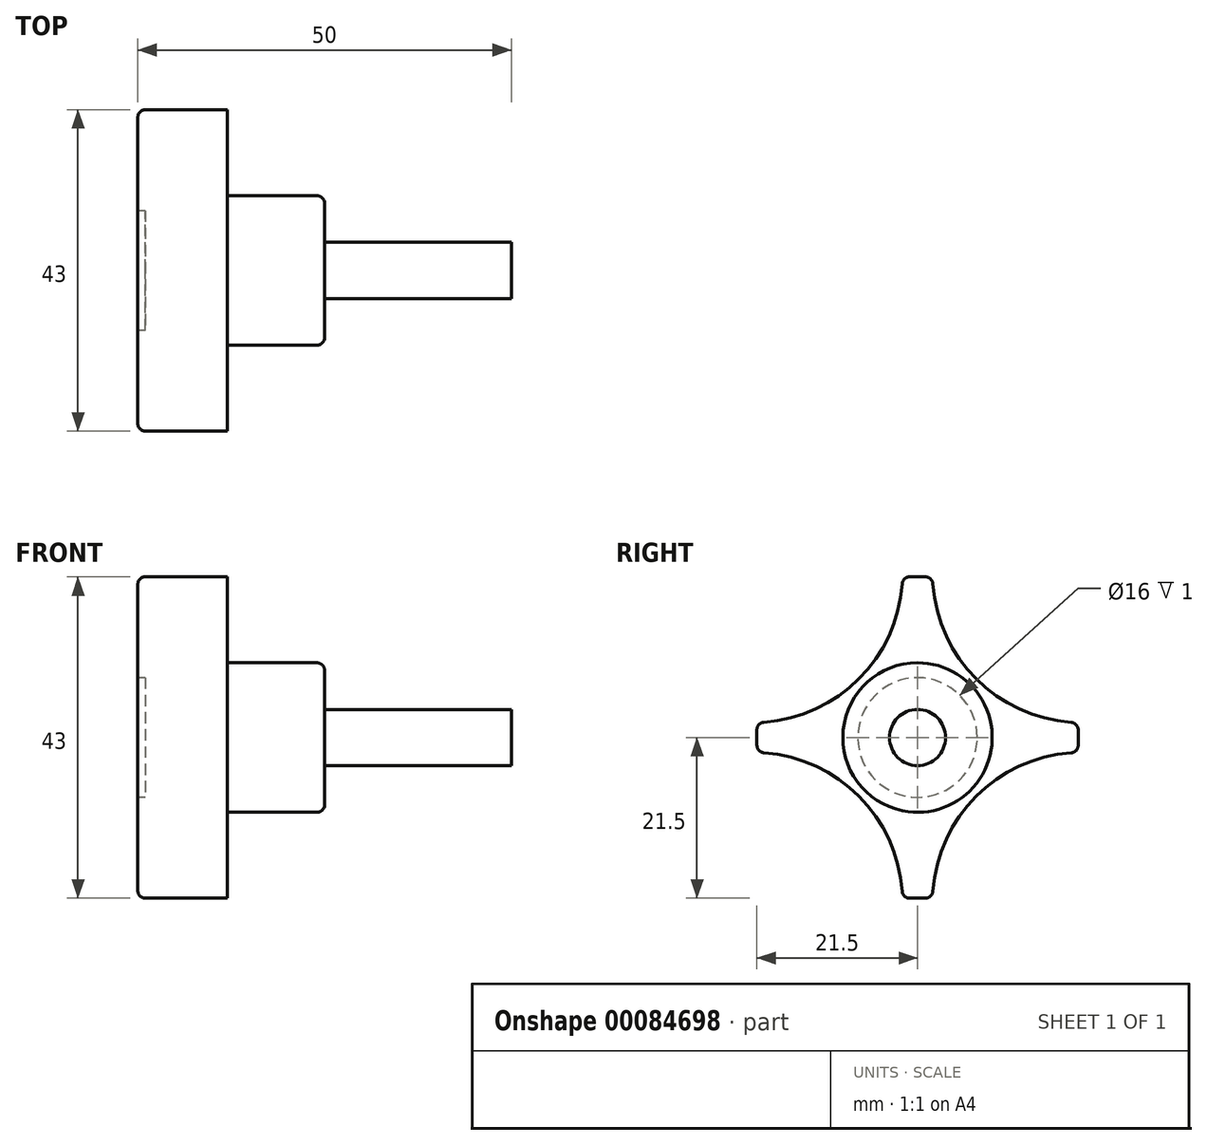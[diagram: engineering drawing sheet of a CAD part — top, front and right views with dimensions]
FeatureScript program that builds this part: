
annotation { "Feature Type Name" : "Feature", "Feature Type Description" : "" }
export const myFeature = defineFeature(function(context is Context, id is Id, definition is map)
    precondition{}
    {
        {
            var Q0;
            Q0=qCreatedBy(makeId("Right.planeOp"),FACE);
            var sketch = newSketch(context, id + "F0", { "sketchPlane" : qUnion([Q0])});
            skCircle(sketch, "E0", {"center": v(0, 0) * mm, "radius": 3.75 * mm});
            skSolve(sketch);
        }
        {
            var Q0;
            Q0 = qSketchRegion(id + "F0", true);
            extrude(context, id + "F1", {"entities" : qUnion([Q0]), "oppositeDirection" : true, "depth" : 25 * mm});
        }
        {
            var Q0;
            Q0=makeQuery(id+"F1.opExtrude","CAP_FACE",FACE,{"disambiguationData":[OSD([sQuery(id+"F0.wireOp",EDGE,"E0")])],"isStart":false});
            var sketch = newSketch(context, id + "F2", { "sketchPlane" : qUnion([Q0])});
            skCircle(sketch, "E1", {"center": v(0, 0) * mm, "radius": 10 * mm});
            skSolve(sketch);
        }
        {
            var Q0;
            Q0 = qSketchRegion(id + "F2", true);
            extrude(context, id + "F3", {"entities" : qUnion([Q0]), "operationType" : NewBodyOperationType.ADD, "depth" : 13 * mm});
        }
        {
            var Q0;
            Q0=makeQuery(id+"F3.opExtrude","CAP_FACE",FACE,{"disambiguationData":[OSD([sQuery(id+"F2.wireOp",EDGE,"E1")])],"isStart":false});
            var sketch = newSketch(context, id + "F4", { "sketchPlane" : qUnion([Q0])});
            skPoint(sketch, "E2", {"position": v(-2, 21.5) * mm});
            skLineSegment(sketch, "E3", {"start": v(-2, 21.5) * mm, "end": v(-2, 0) * mm});
            skLineSegment(sketch, "E4", {"start": v(-2, 21.5) * mm, "end": v(2, 21.5) * mm});
            skLineSegment(sketch, "E5", {"start": v(2, 21.5) * mm, "end": v(2, 0) * mm});
            skLineSegment(sketch, "E6.1.0", {"start": v(-21.5, -2) * mm, "end": v(0, -2) * mm});
            skLineSegment(sketch, "E6.1.1", {"start": v(-21.5, 2) * mm, "end": v(0, 2) * mm});
            skLineSegment(sketch, "E6.1.2", {"start": v(-21.5, -2) * mm, "end": v(-21.5, 2) * mm});
            skLineSegment(sketch, "E6.2.0", {"start": v(2, -21.5) * mm, "end": v(2, 0) * mm});
            skLineSegment(sketch, "E6.2.1", {"start": v(-2, -21.5) * mm, "end": v(-2, 0) * mm});
            skLineSegment(sketch, "E6.2.2", {"start": v(2, -21.5) * mm, "end": v(-2, -21.5) * mm});
            skLineSegment(sketch, "E6.3.0", {"start": v(21.5, 2) * mm, "end": v(0, 2) * mm});
            skLineSegment(sketch, "E6.3.1", {"start": v(21.5, -2) * mm, "end": v(0, -2) * mm});
            skLineSegment(sketch, "E6.3.2", {"start": v(21.5, 2) * mm, "end": v(21.5, -2) * mm});
            skPoint(sketch, "E6.center", {"position": v(0, 0) * mm});
            skSolve(sketch);
        }
        {
            var Q0;
            {var subQ0=sQuery(id+"F4.wireOp",EDGE,"E4");Q0=makeQuery(id+"F4.imprint","IMPRINT",FACE,{"disambiguationData":[TD([[makeQuery(id+"F4.imprint","IMPRINT",EDGE,{"derivedFrom":subQ0}),-1.0]])]});}
            var Q1;
            {var subQ1=sQuery(id+"F4.wireOp",EDGE,"E6.1.1");var subQ3=sQuery(id+"F4.wireOp",EDGE,"E3");var subQ4=makeQuery(id+"F4.imprint","INTERSECT",VERTEX,{"derivedFrom":[subQ3,subQ1]});Q1=makeQuery(id+"F4.imprint","IMPRINT",FACE,{"disambiguationData":[TD([[makeQuery(id+"F4.imprint","IMPRINT",EDGE,{"disambiguationData":[TD([[subQ4,1.0]])],"derivedFrom":subQ3}),1.0]])]});}
            var Q2;
            {var subQ1=sQuery(id+"F4.wireOp",EDGE,"E3");var subQ5=sQuery(id+"F4.wireOp",EDGE,"E6.2.1");var subQ6=makeQuery(id+"F4.imprint","INTERSECT",VERTEX,{"derivedFrom":[subQ1,subQ5]});Q2=makeQuery(id+"F4.imprint","IMPRINT",FACE,{"disambiguationData":[TD([[makeQuery(id+"F4.imprint","IMPRINT",EDGE,{"disambiguationData":[TD([[subQ6,1.0]])],"derivedFrom":subQ1}),-1.0]])]});}
            var Q3;
            {var subQ0=sQuery(id+"F4.wireOp",EDGE,"E6.1.2");Q3=makeQuery(id+"F4.imprint","IMPRINT",FACE,{"disambiguationData":[TD([[makeQuery(id+"F4.imprint","IMPRINT",EDGE,{"derivedFrom":subQ0}),-1.0]])]});}
            var Q4;
            {var subQ1=sQuery(id+"F4.wireOp",EDGE,"E6.1.0");var subQ7=sQuery(id+"F4.wireOp",EDGE,"E6.3.1");var subQ8=makeQuery(id+"F4.imprint","INTERSECT",VERTEX,{"derivedFrom":[subQ1,subQ7]});Q4=makeQuery(id+"F4.imprint","IMPRINT",FACE,{"disambiguationData":[TD([[makeQuery(id+"F4.imprint","IMPRINT",EDGE,{"disambiguationData":[TD([[subQ8,1.0]])],"derivedFrom":subQ1}),-1.0]])]});}
            var Q5;
            {var subQ3=sQuery(id+"F4.wireOp",EDGE,"E3");var subQ8=sQuery(id+"F4.wireOp",EDGE,"E6.2.1");var subQ14=makeQuery(id+"F4.imprint","INTERSECT",VERTEX,{"derivedFrom":[subQ3,subQ8]});Q5=makeQuery(id+"F4.imprint","IMPRINT",FACE,{"disambiguationData":[TD([[makeQuery(id+"F4.imprint","IMPRINT",EDGE,{"disambiguationData":[TD([[subQ14,1.0]])],"derivedFrom":subQ3}),1.0]])]});}
            var Q6;
            {var subQ1=sQuery(id+"F4.wireOp",EDGE,"E5");var subQ7=sQuery(id+"F4.wireOp",EDGE,"E6.2.0");var subQ8=makeQuery(id+"F4.imprint","INTERSECT",VERTEX,{"derivedFrom":[subQ1,subQ7]});Q6=makeQuery(id+"F4.imprint","IMPRINT",FACE,{"disambiguationData":[TD([[makeQuery(id+"F4.imprint","IMPRINT",EDGE,{"disambiguationData":[TD([[subQ8,1.0]])],"derivedFrom":subQ1}),1.0]])]});}
            var Q7;
            {var subQ0=sQuery(id+"F4.wireOp",EDGE,"E6.3.2");Q7=makeQuery(id+"F4.imprint","IMPRINT",FACE,{"disambiguationData":[TD([[makeQuery(id+"F4.imprint","IMPRINT",EDGE,{"derivedFrom":subQ0}),-1.0]])]});}
            var Q8;
            {var subQ0=sQuery(id+"F4.wireOp",EDGE,"E6.2.2");Q8=makeQuery(id+"F4.imprint","IMPRINT",FACE,{"disambiguationData":[TD([[makeQuery(id+"F4.imprint","IMPRINT",EDGE,{"derivedFrom":subQ0}),-1.0]])]});}
            extrude(context, id + "F5", {"entities" : qUnion([Q0, Q1, Q2, Q3, Q4, Q5, Q6, Q7, Q8]), "operationType" : NewBodyOperationType.ADD, "depth" : 12 * mm});
        }
        {
            var Q0;
            Q0=makeQuery(id+"F5.opExtrude","SWEPT_EDGE",EDGE,{"disambiguationData":[OSD([sQuery(id+"F4.wireOp",EDGE,"E6.1.0"),sQuery(id+"F4.wireOp",EDGE,"E6.2.1")])]});
            var Q1;
            Q1=makeQuery(id+"F5.opExtrude","SWEPT_EDGE",EDGE,{"disambiguationData":[OSD([sQuery(id+"F4.wireOp",EDGE,"E6.2.0"),sQuery(id+"F4.wireOp",EDGE,"E6.3.1")])]});
            var Q2;
            Q2=makeQuery(id+"F5.opExtrude","SWEPT_EDGE",EDGE,{"disambiguationData":[OSD([sQuery(id+"F4.wireOp",EDGE,"E5"),sQuery(id+"F4.wireOp",EDGE,"E6.3.0")])]});
            var Q3;
            Q3=makeQuery(id+"F5.opExtrude","SWEPT_EDGE",EDGE,{"disambiguationData":[OSD([sQuery(id+"F4.wireOp",EDGE,"E3"),sQuery(id+"F4.wireOp",EDGE,"E6.1.1")])]});
            fillet(context, id + "F6", {"entities" : qUnion([Q0, Q1, Q2, Q3]), "radius" : 20 * mm, "tangentPropagation" : true, "allowEdgeOverflow" : false});
        }
        {
            var Q0;
            Q0=makeQuery(id+"F6.opFillet","BLEND_EDGE",EDGE,{"blendedFrom":[makeQuery(id+"F5.opExtrude","SWEPT_EDGE",EDGE,{"disambiguationData":[OSD([sQuery(id+"F4.wireOp",EDGE,"E3"),sQuery(id+"F4.wireOp",EDGE,"E6.1.1")])]}),makeQuery(id+"F5.opExtrude","SWEPT_FACE",FACE,{"disambiguationData":[OSD([sQuery(id+"F4.wireOp",EDGE,"E4")])]})],"blendedInto":[makeQuery(id+"F5.opExtrude","SWEPT_FACE",FACE,{"disambiguationData":[OSD([sQuery(id+"F4.wireOp",EDGE,"E4")])]})]});
            var Q1;
            Q1=makeQuery(id+"F6.opFillet","BLEND_EDGE",EDGE,{"blendedFrom":[makeQuery(id+"F5.opExtrude","SWEPT_EDGE",EDGE,{"disambiguationData":[OSD([sQuery(id+"F4.wireOp",EDGE,"E5"),sQuery(id+"F4.wireOp",EDGE,"E6.3.0")])]}),makeQuery(id+"F5.opExtrude","SWEPT_FACE",FACE,{"disambiguationData":[OSD([sQuery(id+"F4.wireOp",EDGE,"E4")])]})],"blendedInto":[makeQuery(id+"F5.opExtrude","SWEPT_FACE",FACE,{"disambiguationData":[OSD([sQuery(id+"F4.wireOp",EDGE,"E4")])]})]});
            var Q2;
            Q2=makeQuery(id+"F6.opFillet","BLEND_EDGE",EDGE,{"blendedFrom":[makeQuery(id+"F5.opExtrude","SWEPT_EDGE",EDGE,{"disambiguationData":[OSD([sQuery(id+"F4.wireOp",EDGE,"E5"),sQuery(id+"F4.wireOp",EDGE,"E6.3.0")])]}),makeQuery(id+"F5.opExtrude","SWEPT_FACE",FACE,{"disambiguationData":[OSD([sQuery(id+"F4.wireOp",EDGE,"E6.3.2")])]})],"blendedInto":[makeQuery(id+"F5.opExtrude","SWEPT_FACE",FACE,{"disambiguationData":[OSD([sQuery(id+"F4.wireOp",EDGE,"E6.3.2")])]})]});
            var Q3;
            Q3=makeQuery(id+"F6.opFillet","BLEND_EDGE",EDGE,{"blendedFrom":[makeQuery(id+"F5.opExtrude","SWEPT_EDGE",EDGE,{"disambiguationData":[OSD([sQuery(id+"F4.wireOp",EDGE,"E3"),sQuery(id+"F4.wireOp",EDGE,"E6.1.1")])]}),makeQuery(id+"F5.opExtrude","SWEPT_FACE",FACE,{"disambiguationData":[OSD([sQuery(id+"F4.wireOp",EDGE,"E6.1.2")])]})],"blendedInto":[makeQuery(id+"F5.opExtrude","SWEPT_FACE",FACE,{"disambiguationData":[OSD([sQuery(id+"F4.wireOp",EDGE,"E6.1.2")])]})]});
            var Q4;
            Q4=makeQuery(id+"F6.opFillet","BLEND_EDGE",EDGE,{"blendedFrom":[makeQuery(id+"F5.opExtrude","SWEPT_EDGE",EDGE,{"disambiguationData":[OSD([sQuery(id+"F4.wireOp",EDGE,"E6.1.0"),sQuery(id+"F4.wireOp",EDGE,"E6.2.1")])]}),makeQuery(id+"F5.opExtrude","SWEPT_FACE",FACE,{"disambiguationData":[OSD([sQuery(id+"F4.wireOp",EDGE,"E6.1.2")])]})],"blendedInto":[makeQuery(id+"F5.opExtrude","SWEPT_FACE",FACE,{"disambiguationData":[OSD([sQuery(id+"F4.wireOp",EDGE,"E6.1.2")])]})]});
            var Q5;
            Q5=makeQuery(id+"F6.opFillet","BLEND_EDGE",EDGE,{"blendedFrom":[makeQuery(id+"F5.opExtrude","SWEPT_EDGE",EDGE,{"disambiguationData":[OSD([sQuery(id+"F4.wireOp",EDGE,"E6.1.0"),sQuery(id+"F4.wireOp",EDGE,"E6.2.1")])]}),makeQuery(id+"F5.opExtrude","SWEPT_FACE",FACE,{"disambiguationData":[OSD([sQuery(id+"F4.wireOp",EDGE,"E6.2.2")])]})],"blendedInto":[makeQuery(id+"F5.opExtrude","SWEPT_FACE",FACE,{"disambiguationData":[OSD([sQuery(id+"F4.wireOp",EDGE,"E6.2.2")])]})]});
            var Q6;
            Q6=makeQuery(id+"F6.opFillet","BLEND_EDGE",EDGE,{"blendedFrom":[makeQuery(id+"F5.opExtrude","SWEPT_EDGE",EDGE,{"disambiguationData":[OSD([sQuery(id+"F4.wireOp",EDGE,"E6.2.0"),sQuery(id+"F4.wireOp",EDGE,"E6.3.1")])]}),makeQuery(id+"F5.opExtrude","SWEPT_FACE",FACE,{"disambiguationData":[OSD([sQuery(id+"F4.wireOp",EDGE,"E6.3.2")])]})],"blendedInto":[makeQuery(id+"F5.opExtrude","SWEPT_FACE",FACE,{"disambiguationData":[OSD([sQuery(id+"F4.wireOp",EDGE,"E6.3.2")])]})]});
            var Q7;
            Q7=makeQuery(id+"F6.opFillet","BLEND_EDGE",EDGE,{"blendedFrom":[makeQuery(id+"F5.opExtrude","SWEPT_EDGE",EDGE,{"disambiguationData":[OSD([sQuery(id+"F4.wireOp",EDGE,"E6.2.0"),sQuery(id+"F4.wireOp",EDGE,"E6.3.1")])]}),makeQuery(id+"F5.opExtrude","SWEPT_FACE",FACE,{"disambiguationData":[OSD([sQuery(id+"F4.wireOp",EDGE,"E6.2.2")])]})],"blendedInto":[makeQuery(id+"F5.opExtrude","SWEPT_FACE",FACE,{"disambiguationData":[OSD([sQuery(id+"F4.wireOp",EDGE,"E6.2.2")])]})]});
            fillet(context, id + "F7", {"entities" : qUnion([Q0, Q1, Q2, Q3, Q4, Q5, Q6, Q7]), "radius" : 1 * mm, "tangentPropagation" : true, "allowEdgeOverflow" : false});
        }
        {
            var Q0;
            Q0=makeQuery(id+"F3.opExtrude","CAP_EDGE",EDGE,{"disambiguationData":[OSD([sQuery(id+"F2.wireOp",EDGE,"E1")])],"isStart":true});
            fillet(context, id + "F8", {"entities" : qUnion([Q0]), "radius" : 1 * mm, "tangentPropagation" : true, "allowEdgeOverflow" : false});
        }
        {
            var Q0;
            Q0=makeQuery(id+"F5.opExtrude","CAP_FACE",FACE,{"disambiguationData":[OSD([sQuery(id+"F4.wireOp",EDGE,"E3"),sQuery(id+"F4.wireOp",EDGE,"E4"),sQuery(id+"F4.wireOp",EDGE,"E5"),sQuery(id+"F4.wireOp",EDGE,"E6.1.0"),sQuery(id+"F4.wireOp",EDGE,"E6.1.1"),sQuery(id+"F4.wireOp",EDGE,"E6.1.2"),sQuery(id+"F4.wireOp",EDGE,"E6.2.0"),sQuery(id+"F4.wireOp",EDGE,"E6.2.1"),sQuery(id+"F4.wireOp",EDGE,"E6.2.2"),sQuery(id+"F4.wireOp",EDGE,"E6.3.0"),sQuery(id+"F4.wireOp",EDGE,"E6.3.1"),sQuery(id+"F4.wireOp",EDGE,"E6.3.2")])],"isStart":false});
            var sketch = newSketch(context, id + "F9", { "sketchPlane" : qUnion([Q0])});
            skCircle(sketch, "E7", {"center": v(0, 0) * mm, "radius": 8 * mm});
            skSolve(sketch);
        }
        {
            var Q0;
            Q0=makeQuery(id+"F9.imprint","IMPRINT",FACE,{"disambiguationData":[TD([[makeQuery(id+"F9.imprint","IMPRINT",EDGE,{"derivedFrom":sQuery(id+"F9.wireOp",EDGE,"E7")}),1.0]])]});
            extrude(context, id + "F10", {"entities" : qUnion([Q0]), "operationType" : NewBodyOperationType.REMOVE, "oppositeDirection" : true, "depth" : 1 * mm});
        }
        {
            var Q0;
            {var subQ0=sQuery(id+"F4.wireOp",EDGE,"E6.1.1");var subQ1=sQuery(id+"F4.wireOp",EDGE,"E3");Q0=makeQuery(id+"F6.opFillet","BLEND_EDGE",EDGE,{"blendedFrom":[makeQuery(id+"F5.opExtrude","SWEPT_EDGE",EDGE,{"disambiguationData":[OSD([subQ1,subQ0])]}),makeQuery(id+"F5.opExtrude","CAP_FACE",FACE,{"disambiguationData":[OSD([subQ1,sQuery(id+"F4.wireOp",EDGE,"E4"),sQuery(id+"F4.wireOp",EDGE,"E5"),sQuery(id+"F4.wireOp",EDGE,"E6.1.0"),subQ0,sQuery(id+"F4.wireOp",EDGE,"E6.1.2"),sQuery(id+"F4.wireOp",EDGE,"E6.2.0"),sQuery(id+"F4.wireOp",EDGE,"E6.2.1"),sQuery(id+"F4.wireOp",EDGE,"E6.2.2"),sQuery(id+"F4.wireOp",EDGE,"E6.3.0"),sQuery(id+"F4.wireOp",EDGE,"E6.3.1"),sQuery(id+"F4.wireOp",EDGE,"E6.3.2")])],"isStart":false})],"blendedInto":[makeQuery(id+"F5.opExtrude","CAP_FACE",FACE,{"disambiguationData":[OSD([subQ1,sQuery(id+"F4.wireOp",EDGE,"E4"),sQuery(id+"F4.wireOp",EDGE,"E5"),sQuery(id+"F4.wireOp",EDGE,"E6.1.0"),subQ0,sQuery(id+"F4.wireOp",EDGE,"E6.1.2"),sQuery(id+"F4.wireOp",EDGE,"E6.2.0"),sQuery(id+"F4.wireOp",EDGE,"E6.2.1"),sQuery(id+"F4.wireOp",EDGE,"E6.2.2"),sQuery(id+"F4.wireOp",EDGE,"E6.3.0"),sQuery(id+"F4.wireOp",EDGE,"E6.3.1"),sQuery(id+"F4.wireOp",EDGE,"E6.3.2")])],"isStart":false})]});}
            var Q1;
            {var subQ0=sQuery(id+"F4.wireOp",EDGE,"E6.3.0");var subQ1=sQuery(id+"F4.wireOp",EDGE,"E5");Q1=makeQuery(id+"F6.opFillet","BLEND_EDGE",EDGE,{"blendedFrom":[makeQuery(id+"F5.opExtrude","SWEPT_EDGE",EDGE,{"disambiguationData":[OSD([subQ1,subQ0])]}),makeQuery(id+"F5.opExtrude","CAP_FACE",FACE,{"disambiguationData":[OSD([sQuery(id+"F4.wireOp",EDGE,"E3"),sQuery(id+"F4.wireOp",EDGE,"E4"),subQ1,sQuery(id+"F4.wireOp",EDGE,"E6.1.0"),sQuery(id+"F4.wireOp",EDGE,"E6.1.1"),sQuery(id+"F4.wireOp",EDGE,"E6.1.2"),sQuery(id+"F4.wireOp",EDGE,"E6.2.0"),sQuery(id+"F4.wireOp",EDGE,"E6.2.1"),sQuery(id+"F4.wireOp",EDGE,"E6.2.2"),subQ0,sQuery(id+"F4.wireOp",EDGE,"E6.3.1"),sQuery(id+"F4.wireOp",EDGE,"E6.3.2")])],"isStart":false})],"blendedInto":[makeQuery(id+"F5.opExtrude","CAP_FACE",FACE,{"disambiguationData":[OSD([sQuery(id+"F4.wireOp",EDGE,"E3"),sQuery(id+"F4.wireOp",EDGE,"E4"),subQ1,sQuery(id+"F4.wireOp",EDGE,"E6.1.0"),sQuery(id+"F4.wireOp",EDGE,"E6.1.1"),sQuery(id+"F4.wireOp",EDGE,"E6.1.2"),sQuery(id+"F4.wireOp",EDGE,"E6.2.0"),sQuery(id+"F4.wireOp",EDGE,"E6.2.1"),sQuery(id+"F4.wireOp",EDGE,"E6.2.2"),subQ0,sQuery(id+"F4.wireOp",EDGE,"E6.3.1"),sQuery(id+"F4.wireOp",EDGE,"E6.3.2")])],"isStart":false})]});}
            var Q2;
            {var subQ0=sQuery(id+"F4.wireOp",EDGE,"E6.3.1");var subQ1=sQuery(id+"F4.wireOp",EDGE,"E6.2.0");Q2=makeQuery(id+"F6.opFillet","BLEND_EDGE",EDGE,{"blendedFrom":[makeQuery(id+"F5.opExtrude","SWEPT_EDGE",EDGE,{"disambiguationData":[OSD([subQ1,subQ0])]}),makeQuery(id+"F5.opExtrude","CAP_FACE",FACE,{"disambiguationData":[OSD([sQuery(id+"F4.wireOp",EDGE,"E3"),sQuery(id+"F4.wireOp",EDGE,"E4"),sQuery(id+"F4.wireOp",EDGE,"E5"),sQuery(id+"F4.wireOp",EDGE,"E6.1.0"),sQuery(id+"F4.wireOp",EDGE,"E6.1.1"),sQuery(id+"F4.wireOp",EDGE,"E6.1.2"),subQ1,sQuery(id+"F4.wireOp",EDGE,"E6.2.1"),sQuery(id+"F4.wireOp",EDGE,"E6.2.2"),sQuery(id+"F4.wireOp",EDGE,"E6.3.0"),subQ0,sQuery(id+"F4.wireOp",EDGE,"E6.3.2")])],"isStart":false})],"blendedInto":[makeQuery(id+"F5.opExtrude","CAP_FACE",FACE,{"disambiguationData":[OSD([sQuery(id+"F4.wireOp",EDGE,"E3"),sQuery(id+"F4.wireOp",EDGE,"E4"),sQuery(id+"F4.wireOp",EDGE,"E5"),sQuery(id+"F4.wireOp",EDGE,"E6.1.0"),sQuery(id+"F4.wireOp",EDGE,"E6.1.1"),sQuery(id+"F4.wireOp",EDGE,"E6.1.2"),subQ1,sQuery(id+"F4.wireOp",EDGE,"E6.2.1"),sQuery(id+"F4.wireOp",EDGE,"E6.2.2"),sQuery(id+"F4.wireOp",EDGE,"E6.3.0"),subQ0,sQuery(id+"F4.wireOp",EDGE,"E6.3.2")])],"isStart":false})]});}
            var Q3;
            {var subQ0=sQuery(id+"F4.wireOp",EDGE,"E6.2.1");var subQ1=sQuery(id+"F4.wireOp",EDGE,"E6.1.0");Q3=makeQuery(id+"F6.opFillet","BLEND_EDGE",EDGE,{"blendedFrom":[makeQuery(id+"F5.opExtrude","SWEPT_EDGE",EDGE,{"disambiguationData":[OSD([subQ1,subQ0])]}),makeQuery(id+"F5.opExtrude","CAP_FACE",FACE,{"disambiguationData":[OSD([sQuery(id+"F4.wireOp",EDGE,"E3"),sQuery(id+"F4.wireOp",EDGE,"E4"),sQuery(id+"F4.wireOp",EDGE,"E5"),subQ1,sQuery(id+"F4.wireOp",EDGE,"E6.1.1"),sQuery(id+"F4.wireOp",EDGE,"E6.1.2"),sQuery(id+"F4.wireOp",EDGE,"E6.2.0"),subQ0,sQuery(id+"F4.wireOp",EDGE,"E6.2.2"),sQuery(id+"F4.wireOp",EDGE,"E6.3.0"),sQuery(id+"F4.wireOp",EDGE,"E6.3.1"),sQuery(id+"F4.wireOp",EDGE,"E6.3.2")])],"isStart":false})],"blendedInto":[makeQuery(id+"F5.opExtrude","CAP_FACE",FACE,{"disambiguationData":[OSD([sQuery(id+"F4.wireOp",EDGE,"E3"),sQuery(id+"F4.wireOp",EDGE,"E4"),sQuery(id+"F4.wireOp",EDGE,"E5"),subQ1,sQuery(id+"F4.wireOp",EDGE,"E6.1.1"),sQuery(id+"F4.wireOp",EDGE,"E6.1.2"),sQuery(id+"F4.wireOp",EDGE,"E6.2.0"),subQ0,sQuery(id+"F4.wireOp",EDGE,"E6.2.2"),sQuery(id+"F4.wireOp",EDGE,"E6.3.0"),sQuery(id+"F4.wireOp",EDGE,"E6.3.1"),sQuery(id+"F4.wireOp",EDGE,"E6.3.2")])],"isStart":false})]});}
            var Q4;
            {var subQ0=sQuery(id+"F4.wireOp",EDGE,"E6.1.1");var subQ1=sQuery(id+"F4.wireOp",EDGE,"E4");var subQ2=sQuery(id+"F4.wireOp",EDGE,"E3");Q4=makeQuery(id+"F7.opFillet","BLEND_EDGE",EDGE,{"blendedFrom":[makeQuery(id+"F6.opFillet","BLEND_EDGE",EDGE,{"blendedFrom":[makeQuery(id+"F5.opExtrude","SWEPT_EDGE",EDGE,{"disambiguationData":[OSD([subQ2,subQ0])]}),makeQuery(id+"F5.opExtrude","SWEPT_FACE",FACE,{"disambiguationData":[OSD([subQ1])]})],"blendedInto":[makeQuery(id+"F5.opExtrude","SWEPT_FACE",FACE,{"disambiguationData":[OSD([subQ1])]})]}),makeQuery(id+"F5.opExtrude","CAP_FACE",FACE,{"disambiguationData":[OSD([subQ2,subQ1,sQuery(id+"F4.wireOp",EDGE,"E5"),sQuery(id+"F4.wireOp",EDGE,"E6.1.0"),subQ0,sQuery(id+"F4.wireOp",EDGE,"E6.1.2"),sQuery(id+"F4.wireOp",EDGE,"E6.2.0"),sQuery(id+"F4.wireOp",EDGE,"E6.2.1"),sQuery(id+"F4.wireOp",EDGE,"E6.2.2"),sQuery(id+"F4.wireOp",EDGE,"E6.3.0"),sQuery(id+"F4.wireOp",EDGE,"E6.3.1"),sQuery(id+"F4.wireOp",EDGE,"E6.3.2")])],"isStart":false})],"blendedInto":[makeQuery(id+"F5.opExtrude","CAP_FACE",FACE,{"disambiguationData":[OSD([subQ2,subQ1,sQuery(id+"F4.wireOp",EDGE,"E5"),sQuery(id+"F4.wireOp",EDGE,"E6.1.0"),subQ0,sQuery(id+"F4.wireOp",EDGE,"E6.1.2"),sQuery(id+"F4.wireOp",EDGE,"E6.2.0"),sQuery(id+"F4.wireOp",EDGE,"E6.2.1"),sQuery(id+"F4.wireOp",EDGE,"E6.2.2"),sQuery(id+"F4.wireOp",EDGE,"E6.3.0"),sQuery(id+"F4.wireOp",EDGE,"E6.3.1"),sQuery(id+"F4.wireOp",EDGE,"E6.3.2")])],"isStart":false})]});}
            var Q5;
            Q5=makeQuery(id+"F5.opExtrude","CAP_EDGE",EDGE,{"disambiguationData":[OSD([sQuery(id+"F4.wireOp",EDGE,"E6.3.2")])],"isStart":false});
            var Q6;
            {var subQ0=sQuery(id+"F4.wireOp",EDGE,"E6.3.0");var subQ1=sQuery(id+"F4.wireOp",EDGE,"E5");var subQ2=sQuery(id+"F4.wireOp",EDGE,"E4");Q6=makeQuery(id+"F7.opFillet","BLEND_EDGE",EDGE,{"blendedFrom":[makeQuery(id+"F6.opFillet","BLEND_EDGE",EDGE,{"blendedFrom":[makeQuery(id+"F5.opExtrude","SWEPT_EDGE",EDGE,{"disambiguationData":[OSD([subQ1,subQ0])]}),makeQuery(id+"F5.opExtrude","SWEPT_FACE",FACE,{"disambiguationData":[OSD([subQ2])]})],"blendedInto":[makeQuery(id+"F5.opExtrude","SWEPT_FACE",FACE,{"disambiguationData":[OSD([subQ2])]})]}),makeQuery(id+"F5.opExtrude","CAP_FACE",FACE,{"disambiguationData":[OSD([sQuery(id+"F4.wireOp",EDGE,"E3"),subQ2,subQ1,sQuery(id+"F4.wireOp",EDGE,"E6.1.0"),sQuery(id+"F4.wireOp",EDGE,"E6.1.1"),sQuery(id+"F4.wireOp",EDGE,"E6.1.2"),sQuery(id+"F4.wireOp",EDGE,"E6.2.0"),sQuery(id+"F4.wireOp",EDGE,"E6.2.1"),sQuery(id+"F4.wireOp",EDGE,"E6.2.2"),subQ0,sQuery(id+"F4.wireOp",EDGE,"E6.3.1"),sQuery(id+"F4.wireOp",EDGE,"E6.3.2")])],"isStart":false})],"blendedInto":[makeQuery(id+"F5.opExtrude","CAP_FACE",FACE,{"disambiguationData":[OSD([sQuery(id+"F4.wireOp",EDGE,"E3"),subQ2,subQ1,sQuery(id+"F4.wireOp",EDGE,"E6.1.0"),sQuery(id+"F4.wireOp",EDGE,"E6.1.1"),sQuery(id+"F4.wireOp",EDGE,"E6.1.2"),sQuery(id+"F4.wireOp",EDGE,"E6.2.0"),sQuery(id+"F4.wireOp",EDGE,"E6.2.1"),sQuery(id+"F4.wireOp",EDGE,"E6.2.2"),subQ0,sQuery(id+"F4.wireOp",EDGE,"E6.3.1"),sQuery(id+"F4.wireOp",EDGE,"E6.3.2")])],"isStart":false})]});}
            var Q7;
            Q7=makeQuery(id+"F5.opExtrude","CAP_EDGE",EDGE,{"disambiguationData":[OSD([sQuery(id+"F4.wireOp",EDGE,"E4")])],"isStart":false});
            var Q8;
            {var subQ0=sQuery(id+"F4.wireOp",EDGE,"E6.2.1");var subQ1=sQuery(id+"F4.wireOp",EDGE,"E6.1.2");var subQ2=sQuery(id+"F4.wireOp",EDGE,"E6.1.0");Q8=makeQuery(id+"F7.opFillet","BLEND_EDGE",EDGE,{"blendedFrom":[makeQuery(id+"F6.opFillet","BLEND_EDGE",EDGE,{"blendedFrom":[makeQuery(id+"F5.opExtrude","SWEPT_EDGE",EDGE,{"disambiguationData":[OSD([subQ2,subQ0])]}),makeQuery(id+"F5.opExtrude","SWEPT_FACE",FACE,{"disambiguationData":[OSD([subQ1])]})],"blendedInto":[makeQuery(id+"F5.opExtrude","SWEPT_FACE",FACE,{"disambiguationData":[OSD([subQ1])]})]}),makeQuery(id+"F5.opExtrude","CAP_FACE",FACE,{"disambiguationData":[OSD([sQuery(id+"F4.wireOp",EDGE,"E3"),sQuery(id+"F4.wireOp",EDGE,"E4"),sQuery(id+"F4.wireOp",EDGE,"E5"),subQ2,sQuery(id+"F4.wireOp",EDGE,"E6.1.1"),subQ1,sQuery(id+"F4.wireOp",EDGE,"E6.2.0"),subQ0,sQuery(id+"F4.wireOp",EDGE,"E6.2.2"),sQuery(id+"F4.wireOp",EDGE,"E6.3.0"),sQuery(id+"F4.wireOp",EDGE,"E6.3.1"),sQuery(id+"F4.wireOp",EDGE,"E6.3.2")])],"isStart":false})],"blendedInto":[makeQuery(id+"F5.opExtrude","CAP_FACE",FACE,{"disambiguationData":[OSD([sQuery(id+"F4.wireOp",EDGE,"E3"),sQuery(id+"F4.wireOp",EDGE,"E4"),sQuery(id+"F4.wireOp",EDGE,"E5"),subQ2,sQuery(id+"F4.wireOp",EDGE,"E6.1.1"),subQ1,sQuery(id+"F4.wireOp",EDGE,"E6.2.0"),subQ0,sQuery(id+"F4.wireOp",EDGE,"E6.2.2"),sQuery(id+"F4.wireOp",EDGE,"E6.3.0"),sQuery(id+"F4.wireOp",EDGE,"E6.3.1"),sQuery(id+"F4.wireOp",EDGE,"E6.3.2")])],"isStart":false})]});}
            var Q9;
            Q9=makeQuery(id+"F5.opExtrude","CAP_EDGE",EDGE,{"disambiguationData":[OSD([sQuery(id+"F4.wireOp",EDGE,"E6.1.2")])],"isStart":false});
            var Q10;
            {var subQ0=sQuery(id+"F4.wireOp",EDGE,"E6.1.2");var subQ1=sQuery(id+"F4.wireOp",EDGE,"E6.1.1");var subQ2=sQuery(id+"F4.wireOp",EDGE,"E3");Q10=makeQuery(id+"F7.opFillet","BLEND_EDGE",EDGE,{"blendedFrom":[makeQuery(id+"F6.opFillet","BLEND_EDGE",EDGE,{"blendedFrom":[makeQuery(id+"F5.opExtrude","SWEPT_EDGE",EDGE,{"disambiguationData":[OSD([subQ2,subQ1])]}),makeQuery(id+"F5.opExtrude","SWEPT_FACE",FACE,{"disambiguationData":[OSD([subQ0])]})],"blendedInto":[makeQuery(id+"F5.opExtrude","SWEPT_FACE",FACE,{"disambiguationData":[OSD([subQ0])]})]}),makeQuery(id+"F5.opExtrude","CAP_FACE",FACE,{"disambiguationData":[OSD([subQ2,sQuery(id+"F4.wireOp",EDGE,"E4"),sQuery(id+"F4.wireOp",EDGE,"E5"),sQuery(id+"F4.wireOp",EDGE,"E6.1.0"),subQ1,subQ0,sQuery(id+"F4.wireOp",EDGE,"E6.2.0"),sQuery(id+"F4.wireOp",EDGE,"E6.2.1"),sQuery(id+"F4.wireOp",EDGE,"E6.2.2"),sQuery(id+"F4.wireOp",EDGE,"E6.3.0"),sQuery(id+"F4.wireOp",EDGE,"E6.3.1"),sQuery(id+"F4.wireOp",EDGE,"E6.3.2")])],"isStart":false})],"blendedInto":[makeQuery(id+"F5.opExtrude","CAP_FACE",FACE,{"disambiguationData":[OSD([subQ2,sQuery(id+"F4.wireOp",EDGE,"E4"),sQuery(id+"F4.wireOp",EDGE,"E5"),sQuery(id+"F4.wireOp",EDGE,"E6.1.0"),subQ1,subQ0,sQuery(id+"F4.wireOp",EDGE,"E6.2.0"),sQuery(id+"F4.wireOp",EDGE,"E6.2.1"),sQuery(id+"F4.wireOp",EDGE,"E6.2.2"),sQuery(id+"F4.wireOp",EDGE,"E6.3.0"),sQuery(id+"F4.wireOp",EDGE,"E6.3.1"),sQuery(id+"F4.wireOp",EDGE,"E6.3.2")])],"isStart":false})]});}
            var Q11;
            {var subQ0=sQuery(id+"F4.wireOp",EDGE,"E6.2.2");var subQ1=sQuery(id+"F4.wireOp",EDGE,"E6.2.1");var subQ2=sQuery(id+"F4.wireOp",EDGE,"E6.1.0");Q11=makeQuery(id+"F7.opFillet","BLEND_EDGE",EDGE,{"blendedFrom":[makeQuery(id+"F6.opFillet","BLEND_EDGE",EDGE,{"blendedFrom":[makeQuery(id+"F5.opExtrude","SWEPT_EDGE",EDGE,{"disambiguationData":[OSD([subQ2,subQ1])]}),makeQuery(id+"F5.opExtrude","SWEPT_FACE",FACE,{"disambiguationData":[OSD([subQ0])]})],"blendedInto":[makeQuery(id+"F5.opExtrude","SWEPT_FACE",FACE,{"disambiguationData":[OSD([subQ0])]})]}),makeQuery(id+"F5.opExtrude","CAP_FACE",FACE,{"disambiguationData":[OSD([sQuery(id+"F4.wireOp",EDGE,"E3"),sQuery(id+"F4.wireOp",EDGE,"E4"),sQuery(id+"F4.wireOp",EDGE,"E5"),subQ2,sQuery(id+"F4.wireOp",EDGE,"E6.1.1"),sQuery(id+"F4.wireOp",EDGE,"E6.1.2"),sQuery(id+"F4.wireOp",EDGE,"E6.2.0"),subQ1,subQ0,sQuery(id+"F4.wireOp",EDGE,"E6.3.0"),sQuery(id+"F4.wireOp",EDGE,"E6.3.1"),sQuery(id+"F4.wireOp",EDGE,"E6.3.2")])],"isStart":false})],"blendedInto":[makeQuery(id+"F5.opExtrude","CAP_FACE",FACE,{"disambiguationData":[OSD([sQuery(id+"F4.wireOp",EDGE,"E3"),sQuery(id+"F4.wireOp",EDGE,"E4"),sQuery(id+"F4.wireOp",EDGE,"E5"),subQ2,sQuery(id+"F4.wireOp",EDGE,"E6.1.1"),sQuery(id+"F4.wireOp",EDGE,"E6.1.2"),sQuery(id+"F4.wireOp",EDGE,"E6.2.0"),subQ1,subQ0,sQuery(id+"F4.wireOp",EDGE,"E6.3.0"),sQuery(id+"F4.wireOp",EDGE,"E6.3.1"),sQuery(id+"F4.wireOp",EDGE,"E6.3.2")])],"isStart":false})]});}
            var Q12;
            Q12=makeQuery(id+"F5.opExtrude","CAP_EDGE",EDGE,{"disambiguationData":[OSD([sQuery(id+"F4.wireOp",EDGE,"E6.2.2")])],"isStart":false});
            var Q13;
            {var subQ0=sQuery(id+"F4.wireOp",EDGE,"E6.3.1");var subQ1=sQuery(id+"F4.wireOp",EDGE,"E6.2.2");var subQ2=sQuery(id+"F4.wireOp",EDGE,"E6.2.0");Q13=makeQuery(id+"F7.opFillet","BLEND_EDGE",EDGE,{"blendedFrom":[makeQuery(id+"F6.opFillet","BLEND_EDGE",EDGE,{"blendedFrom":[makeQuery(id+"F5.opExtrude","SWEPT_EDGE",EDGE,{"disambiguationData":[OSD([subQ2,subQ0])]}),makeQuery(id+"F5.opExtrude","SWEPT_FACE",FACE,{"disambiguationData":[OSD([subQ1])]})],"blendedInto":[makeQuery(id+"F5.opExtrude","SWEPT_FACE",FACE,{"disambiguationData":[OSD([subQ1])]})]}),makeQuery(id+"F5.opExtrude","CAP_FACE",FACE,{"disambiguationData":[OSD([sQuery(id+"F4.wireOp",EDGE,"E3"),sQuery(id+"F4.wireOp",EDGE,"E4"),sQuery(id+"F4.wireOp",EDGE,"E5"),sQuery(id+"F4.wireOp",EDGE,"E6.1.0"),sQuery(id+"F4.wireOp",EDGE,"E6.1.1"),sQuery(id+"F4.wireOp",EDGE,"E6.1.2"),subQ2,sQuery(id+"F4.wireOp",EDGE,"E6.2.1"),subQ1,sQuery(id+"F4.wireOp",EDGE,"E6.3.0"),subQ0,sQuery(id+"F4.wireOp",EDGE,"E6.3.2")])],"isStart":false})],"blendedInto":[makeQuery(id+"F5.opExtrude","CAP_FACE",FACE,{"disambiguationData":[OSD([sQuery(id+"F4.wireOp",EDGE,"E3"),sQuery(id+"F4.wireOp",EDGE,"E4"),sQuery(id+"F4.wireOp",EDGE,"E5"),sQuery(id+"F4.wireOp",EDGE,"E6.1.0"),sQuery(id+"F4.wireOp",EDGE,"E6.1.1"),sQuery(id+"F4.wireOp",EDGE,"E6.1.2"),subQ2,sQuery(id+"F4.wireOp",EDGE,"E6.2.1"),subQ1,sQuery(id+"F4.wireOp",EDGE,"E6.3.0"),subQ0,sQuery(id+"F4.wireOp",EDGE,"E6.3.2")])],"isStart":false})]});}
            var Q14;
            {var subQ0=sQuery(id+"F4.wireOp",EDGE,"E6.3.2");var subQ1=sQuery(id+"F4.wireOp",EDGE,"E6.3.1");var subQ2=sQuery(id+"F4.wireOp",EDGE,"E6.2.0");Q14=makeQuery(id+"F7.opFillet","BLEND_EDGE",EDGE,{"blendedFrom":[makeQuery(id+"F6.opFillet","BLEND_EDGE",EDGE,{"blendedFrom":[makeQuery(id+"F5.opExtrude","SWEPT_EDGE",EDGE,{"disambiguationData":[OSD([subQ2,subQ1])]}),makeQuery(id+"F5.opExtrude","SWEPT_FACE",FACE,{"disambiguationData":[OSD([subQ0])]})],"blendedInto":[makeQuery(id+"F5.opExtrude","SWEPT_FACE",FACE,{"disambiguationData":[OSD([subQ0])]})]}),makeQuery(id+"F5.opExtrude","CAP_FACE",FACE,{"disambiguationData":[OSD([sQuery(id+"F4.wireOp",EDGE,"E3"),sQuery(id+"F4.wireOp",EDGE,"E4"),sQuery(id+"F4.wireOp",EDGE,"E5"),sQuery(id+"F4.wireOp",EDGE,"E6.1.0"),sQuery(id+"F4.wireOp",EDGE,"E6.1.1"),sQuery(id+"F4.wireOp",EDGE,"E6.1.2"),subQ2,sQuery(id+"F4.wireOp",EDGE,"E6.2.1"),sQuery(id+"F4.wireOp",EDGE,"E6.2.2"),sQuery(id+"F4.wireOp",EDGE,"E6.3.0"),subQ1,subQ0])],"isStart":false})],"blendedInto":[makeQuery(id+"F5.opExtrude","CAP_FACE",FACE,{"disambiguationData":[OSD([sQuery(id+"F4.wireOp",EDGE,"E3"),sQuery(id+"F4.wireOp",EDGE,"E4"),sQuery(id+"F4.wireOp",EDGE,"E5"),sQuery(id+"F4.wireOp",EDGE,"E6.1.0"),sQuery(id+"F4.wireOp",EDGE,"E6.1.1"),sQuery(id+"F4.wireOp",EDGE,"E6.1.2"),subQ2,sQuery(id+"F4.wireOp",EDGE,"E6.2.1"),sQuery(id+"F4.wireOp",EDGE,"E6.2.2"),sQuery(id+"F4.wireOp",EDGE,"E6.3.0"),subQ1,subQ0])],"isStart":false})]});}
            var Q15;
            {var subQ0=sQuery(id+"F4.wireOp",EDGE,"E6.3.2");var subQ1=sQuery(id+"F4.wireOp",EDGE,"E6.3.0");var subQ2=sQuery(id+"F4.wireOp",EDGE,"E5");Q15=makeQuery(id+"F7.opFillet","BLEND_EDGE",EDGE,{"blendedFrom":[makeQuery(id+"F6.opFillet","BLEND_EDGE",EDGE,{"blendedFrom":[makeQuery(id+"F5.opExtrude","SWEPT_EDGE",EDGE,{"disambiguationData":[OSD([subQ2,subQ1])]}),makeQuery(id+"F5.opExtrude","SWEPT_FACE",FACE,{"disambiguationData":[OSD([subQ0])]})],"blendedInto":[makeQuery(id+"F5.opExtrude","SWEPT_FACE",FACE,{"disambiguationData":[OSD([subQ0])]})]}),makeQuery(id+"F5.opExtrude","CAP_FACE",FACE,{"disambiguationData":[OSD([sQuery(id+"F4.wireOp",EDGE,"E3"),sQuery(id+"F4.wireOp",EDGE,"E4"),subQ2,sQuery(id+"F4.wireOp",EDGE,"E6.1.0"),sQuery(id+"F4.wireOp",EDGE,"E6.1.1"),sQuery(id+"F4.wireOp",EDGE,"E6.1.2"),sQuery(id+"F4.wireOp",EDGE,"E6.2.0"),sQuery(id+"F4.wireOp",EDGE,"E6.2.1"),sQuery(id+"F4.wireOp",EDGE,"E6.2.2"),subQ1,sQuery(id+"F4.wireOp",EDGE,"E6.3.1"),subQ0])],"isStart":false})],"blendedInto":[makeQuery(id+"F5.opExtrude","CAP_FACE",FACE,{"disambiguationData":[OSD([sQuery(id+"F4.wireOp",EDGE,"E3"),sQuery(id+"F4.wireOp",EDGE,"E4"),subQ2,sQuery(id+"F4.wireOp",EDGE,"E6.1.0"),sQuery(id+"F4.wireOp",EDGE,"E6.1.1"),sQuery(id+"F4.wireOp",EDGE,"E6.1.2"),sQuery(id+"F4.wireOp",EDGE,"E6.2.0"),sQuery(id+"F4.wireOp",EDGE,"E6.2.1"),sQuery(id+"F4.wireOp",EDGE,"E6.2.2"),subQ1,sQuery(id+"F4.wireOp",EDGE,"E6.3.1"),subQ0])],"isStart":false})]});}
            fillet(context, id + "F11", {"entities" : qUnion([Q0, Q1, Q2, Q3, Q4, Q5, Q6, Q7, Q8, Q9, Q10, Q11, Q12, Q13, Q14, Q15]), "radius" : 1 * mm, "tangentPropagation" : true, "allowEdgeOverflow" : false});
        }
    });
